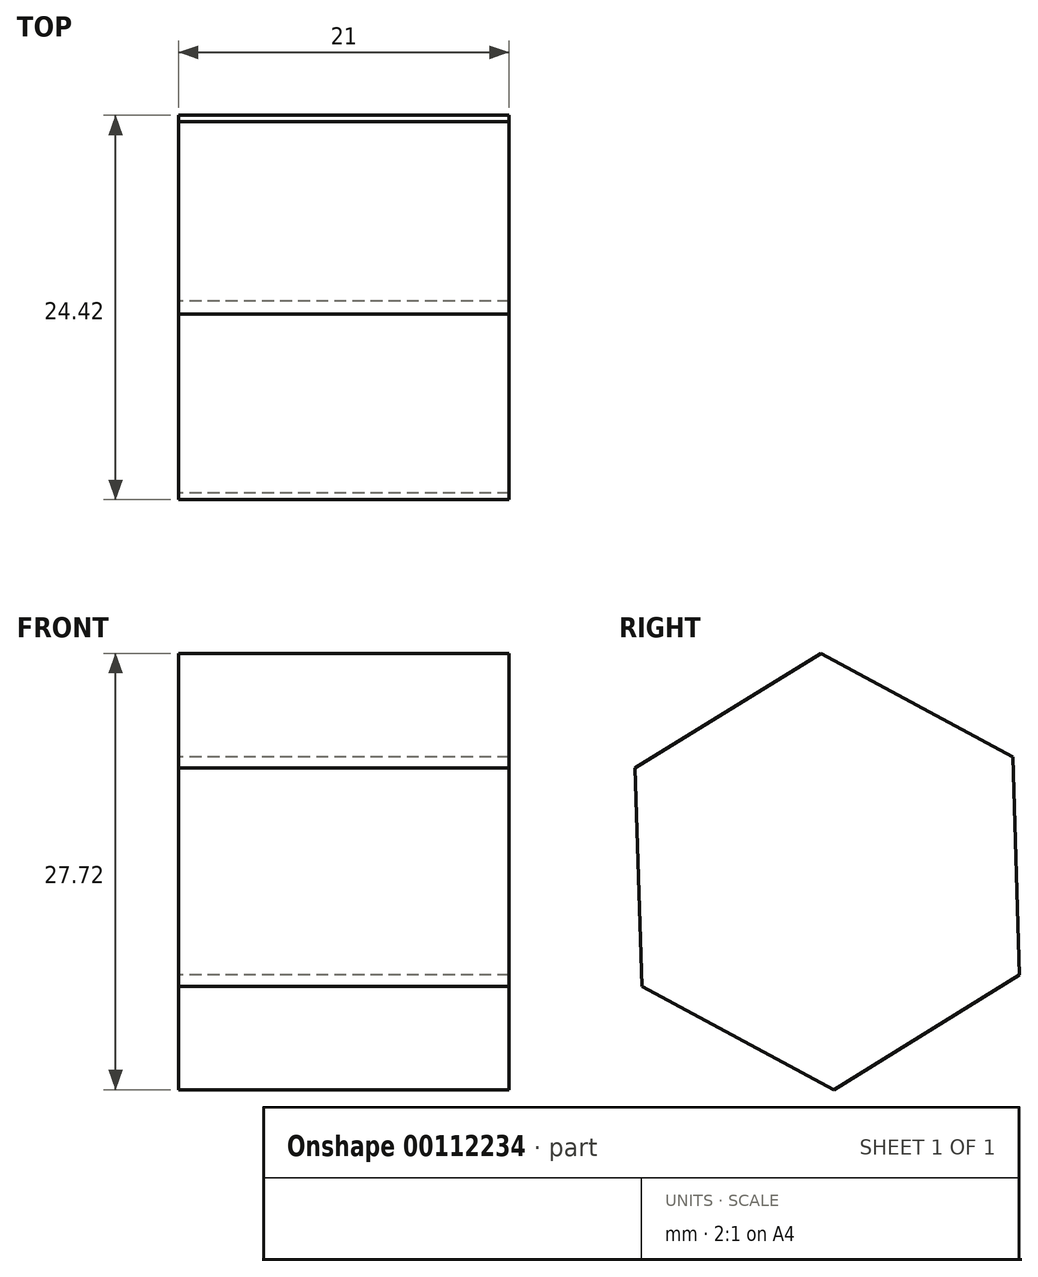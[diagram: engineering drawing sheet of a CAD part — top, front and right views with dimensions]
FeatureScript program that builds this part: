
annotation { "Feature Type Name" : "Feature", "Feature Type Description" : "" }
export const myFeature = defineFeature(function(context is Context, id is Id, definition is map)
    precondition{}
    {
        {
            var Q0;
            Q0=qCreatedBy(makeId("Right.planeOp"),FACE);
            var sketch = newSketch(context, id + "F0", { "sketchPlane" : qUnion([Q0])});
            skCircle(sketch, "E0.cCircle", {"center": v(0, 0) * mm, "radius": 12 * mm, "construction": true});
            skLineSegment(sketch, "E0.0", {"start": v(-0.41, 13.86) * mm, "end": v(11.8, 7.29) * mm});
            skLineSegment(sketch, "E0.1", {"start": v(11.8, 7.29) * mm, "end": v(12.2, -6.57) * mm});
            skLineSegment(sketch, "E0.2", {"start": v(12.2, -6.57) * mm, "end": v(0.41, -13.86) * mm});
            skLineSegment(sketch, "E0.3", {"start": v(0.41, -13.86) * mm, "end": v(-11.8, -7.29) * mm});
            skLineSegment(sketch, "E0.4", {"start": v(-11.8, -7.29) * mm, "end": v(-12.2, 6.57) * mm});
            skLineSegment(sketch, "E0.5", {"start": v(-12.2, 6.57) * mm, "end": v(-0.41, 13.86) * mm});
            skPoint(sketch, "E0.0.midPoint", {"position": v(5.69, 10.57) * mm});
            skSolve(sketch);
        }
        {
            var Q0;
            Q0=makeQuery(id+"F0.imprint","IMPRINT",FACE,{"disambiguationData":[TD([[makeQuery(id+"F0.imprint","IMPRINT",EDGE,{"derivedFrom":sQuery(id+"F0.wireOp",EDGE,"E0.0")}),-1.0]])]});
            extrude(context, id + "F1", {"entities" : qUnion([Q0]), "depth" : 21 * mm});
        }
    });
